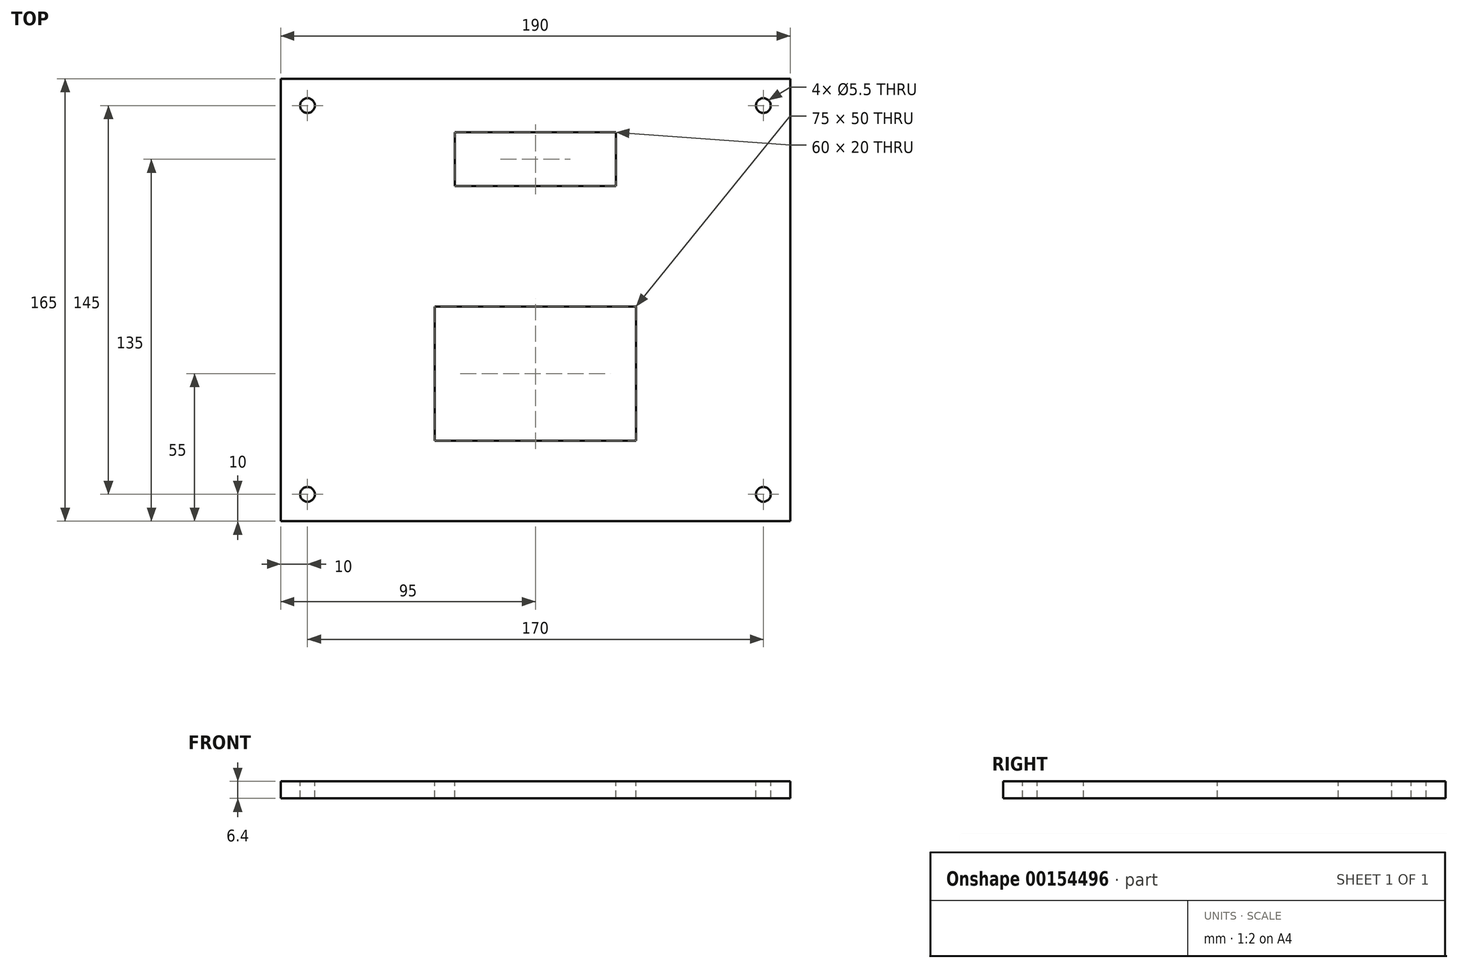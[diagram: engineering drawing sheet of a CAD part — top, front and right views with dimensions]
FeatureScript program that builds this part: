
annotation { "Feature Type Name" : "Feature", "Feature Type Description" : "" }
export const myFeature = defineFeature(function(context is Context, id is Id, definition is map)
    precondition{}
    {
        {
            var Q0;
            Q0=qCreatedBy(makeId("Top.planeOp"),FACE);
            var sketch = newSketch(context, id + "F0", { "sketchPlane" : qUnion([Q0])});
            skLineSegment(sketch, "E0.bottom", {"start": v(-95, 82.5) * mm, "end": v(95, 82.5) * mm});
            skLineSegment(sketch, "E0.top", {"start": v(-95, -82.5) * mm, "end": v(95, -82.5) * mm});
            skLineSegment(sketch, "E0.left", {"start": v(-95, 82.5) * mm, "end": v(-95, -82.5) * mm});
            skLineSegment(sketch, "E0.right", {"start": v(95, 82.5) * mm, "end": v(95, -82.5) * mm});
            skPoint(sketch, "E0.middle", {"position": v(0, 0) * mm});
            skLineSegment(sketch, "E1.bottom", {"start": v(-30, 62.5) * mm, "end": v(30, 62.5) * mm});
            skLineSegment(sketch, "E1.top", {"start": v(-30, 42.5) * mm, "end": v(30, 42.5) * mm});
            skLineSegment(sketch, "E1.left", {"start": v(-30, 62.5) * mm, "end": v(-30, 42.5) * mm});
            skLineSegment(sketch, "E1.right", {"start": v(30, 62.5) * mm, "end": v(30, 42.5) * mm});
            skLineSegment(sketch, "E2", {"start": v(0, 62.5) * mm, "end": v(0, 82.5) * mm, "construction": true});
            skLineSegment(sketch, "E3", {"start": v(-30, 52.5) * mm, "end": v(30, 52.5) * mm, "construction": true});
            skLineSegment(sketch, "E4", {"start": v(0, 42.5) * mm, "end": v(0, 62.5) * mm, "construction": true});
            skLineSegment(sketch, "E5.0", {"start": v(-85, 72.5) * mm, "end": v(85, 72.5) * mm, "construction": true});
            skLineSegment(sketch, "E5.1", {"start": v(-85, 72.5) * mm, "end": v(-85, -72.5) * mm, "construction": true});
            skLineSegment(sketch, "E5.2", {"start": v(-85, -72.5) * mm, "end": v(85, -72.5) * mm, "construction": true});
            skLineSegment(sketch, "E5.3", {"start": v(85, 72.5) * mm, "end": v(85, -72.5) * mm, "construction": true});
            skLineSegment(sketch, "E6.bottom", {"start": v(-37.5, -2.5) * mm, "end": v(37.5, -2.5) * mm});
            skLineSegment(sketch, "E6.top", {"start": v(-37.5, -52.5) * mm, "end": v(37.5, -52.5) * mm});
            skLineSegment(sketch, "E6.left", {"start": v(-37.5, -2.5) * mm, "end": v(-37.5, -52.5) * mm});
            skLineSegment(sketch, "E6.right", {"start": v(37.5, -2.5) * mm, "end": v(37.5, -52.5) * mm});
            skLineSegment(sketch, "E7", {"start": v(0, -52.5) * mm, "end": v(0, -82.5) * mm, "construction": true});
            skSolve(sketch);
        }
        {
            var Q0;
            Q0=makeQuery(id+"F0.imprint","IMPRINT",FACE,{"disambiguationData":[TD([[makeQuery(id+"F0.imprint","IMPRINT",EDGE,{"derivedFrom":sQuery(id+"F0.wireOp",EDGE,"E0.bottom")}),-1.0]])]});
            extrude(context, id + "F1", {"entities" : qUnion([Q0]), "oppositeDirection" : true, "depth" : 6.4 * mm});
        }
        {
            var Q0;
            Q0=sQuery(id+"F0.wireOp",VERTEX,"E5.0.end");
            var Q1;
            Q1=sQuery(id+"F0.wireOp",VERTEX,"E5.0.start");
            var Q2;
            Q2=sQuery(id+"F0.wireOp",VERTEX,"E5.1.end");
            var Q3;
            Q3=sQuery(id+"F0.wireOp",VERTEX,"E5.2.end");
            var Q4;
            Q4=makeQuery(id+"F1.opExtrude","SWEPT_BODY",BODY,{"disambiguationData":[OSD([sQuery(id+"F0.wireOp",EDGE,"E0.bottom"),sQuery(id+"F0.wireOp",EDGE,"E0.top"),sQuery(id+"F0.wireOp",EDGE,"E0.left"),sQuery(id+"F0.wireOp",EDGE,"E0.right"),sQuery(id+"F0.wireOp",EDGE,"E1.bottom"),sQuery(id+"F0.wireOp",EDGE,"E1.top"),sQuery(id+"F0.wireOp",EDGE,"E1.left"),sQuery(id+"F0.wireOp",EDGE,"E1.right"),sQuery(id+"F0.wireOp",EDGE,"E6.bottom"),sQuery(id+"F0.wireOp",EDGE,"E6.top"),sQuery(id+"F0.wireOp",EDGE,"E6.left"),sQuery(id+"F0.wireOp",EDGE,"E6.right")])]});
            hole(context, id + "F2", {"style" : HoleStyle.SIMPLE, "endStyle" : HoleEndStyle.THROUGH, "holeDiameter" : 5.5 * mm, "locations" : qUnion([Q0, Q1, Q2, Q3]), "scope" : qUnion([Q4]), "isTappedThrough" : true});
        }
    });
